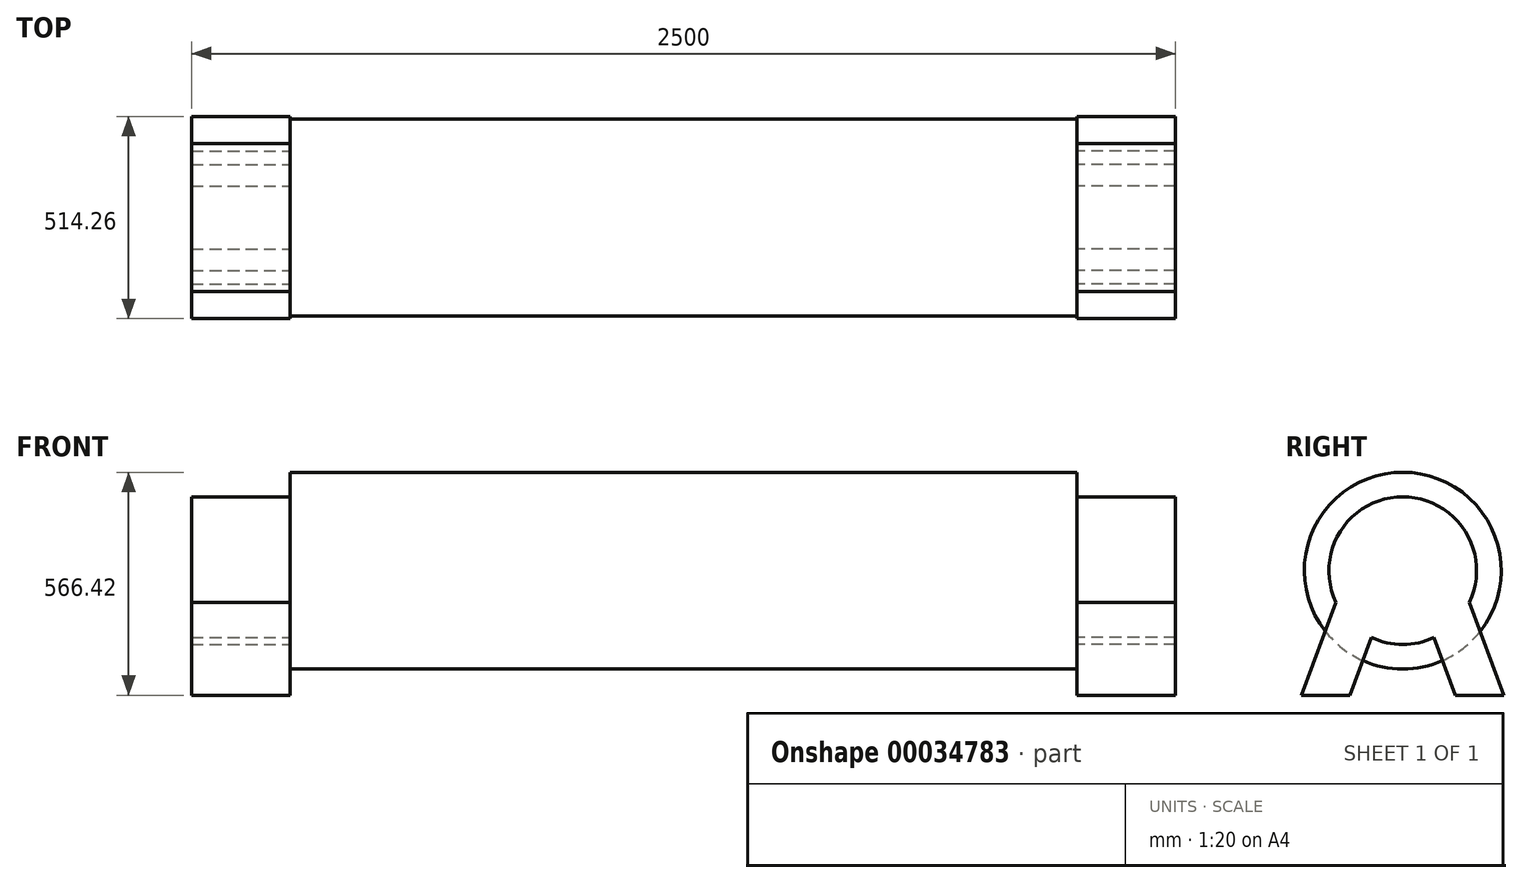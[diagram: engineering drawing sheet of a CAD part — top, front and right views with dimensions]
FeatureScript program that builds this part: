
annotation { "Feature Type Name" : "Feature", "Feature Type Description" : "" }
export const myFeature = defineFeature(function(context is Context, id is Id, definition is map)
    precondition{}
    {
        {
            var Q0;
            Q0=qCreatedBy(makeId("Right.planeOp"),FACE);
            var sketch = newSketch(context, id + "F0", { "sketchPlane" : qUnion([Q0])});
            skCircle(sketch, "E0", {"center": v(0, 0) * mm, "radius": 250 * mm});
            skSolve(sketch);
        }
        {
            var Q0;
            Q0=makeQuery(id+"F0.imprint","IMPRINT",FACE,{"disambiguationData":[TD([[makeQuery(id+"F0.imprint","IMPRINT",EDGE,{"derivedFrom":sQuery(id+"F0.wireOp",EDGE,"E0")}),1.0]])]});
            extrude(context, id + "F1", {"entities" : qUnion([Q0]), "depth" : 2000 * mm});
        }
        {
            var Q0;
            Q0=makeQuery(id+"F1.opExtrude","CAP_FACE",FACE,{"disambiguationData":[OSD([sQuery(id+"F0.wireOp",EDGE,"E0")])],"isStart":false});
            var sketch = newSketch(context, id + "F2", { "sketchPlane" : qUnion([Q0])});
            skCircle(sketch, "E1", {"center": v(0, 0) * mm, "radius": 125 * mm});
            skSolve(sketch);
        }
        {
            var Q0;
            Q0=makeQuery(id+"F2.imprint","IMPRINT",FACE,{"disambiguationData":[TD([[makeQuery(id+"F2.imprint","IMPRINT",EDGE,{"derivedFrom":sQuery(id+"F2.wireOp",EDGE,"E1")}),1.0]])]});
            extrude(context, id + "F3", {"entities" : qUnion([Q0]), "operationType" : NewBodyOperationType.ADD, "depth" : 250 * mm, "hasSecondDirection" : true, "secondDirectionOppositeDirection" : true, "secondDirectionDepth" : 2250 * mm});
        }
        {
            var Q0;
            Q0=makeQuery(id+"F1.opExtrude","CAP_FACE",FACE,{"disambiguationData":[OSD([sQuery(id+"F0.wireOp",EDGE,"E0")])],"isStart":false});
            var sketch = newSketch(context, id + "F4", { "sketchPlane" : qUnion([Q0])});
            skCircle(sketch, "E2", {"center": v(0, 0) * mm, "radius": 187.5 * mm});
            skLineSegment(sketch, "E3", {"start": v(-169.32, -80.55) * mm, "end": v(-257.13, -316.42) * mm});
            skLineSegment(sketch, "E4", {"start": v(-257.13, -316.42) * mm, "end": v(-134.25, -316.42) * mm});
            skLineSegment(sketch, "E5", {"start": v(-134.25, -316.42) * mm, "end": v(-79.64, -169.74) * mm});
            skLineSegment(sketch, "E6", {"start": v(0, 0) * mm, "end": v(0, -613.8) * mm, "construction": true});
            skLineSegment(sketch, "E7.MirrorCS", {"start": v(257.13, -316.42) * mm, "end": v(134.25, -316.42) * mm});
            skLineSegment(sketch, "E8.MirrorCS", {"start": v(169.32, -80.55) * mm, "end": v(257.13, -316.42) * mm});
            skLineSegment(sketch, "E9.MirrorCS", {"start": v(134.25, -316.42) * mm, "end": v(79.64, -169.74) * mm});
            skLineSegment(sketch, "E10", {"start": v(0, -316.42) * mm, "end": v(0, 250) * mm, "construction": true});
            skSolve(sketch);
        }
        {
            var Q0;
            {var subQ5=sQuery(id+"F4.wireOp",EDGE,"E4");Q0=makeQuery(id+"F4.imprint","IMPRINT",FACE,{"disambiguationData":[TD([[makeQuery(id+"F4.imprint","IMPRINT",EDGE,{"derivedFrom":subQ5}),1.0]])]});}
            var Q1;
            {var subQ5=sQuery(id+"F4.wireOp",EDGE,"E7.MirrorCS");Q1=makeQuery(id+"F4.imprint","IMPRINT",FACE,{"disambiguationData":[TD([[makeQuery(id+"F4.imprint","IMPRINT",EDGE,{"derivedFrom":subQ5}),-1.0]])]});}
            var Q2;
            {var subQ3=sQuery(id+"F4.wireOp",EDGE,"E8.MirrorCS");var subQ5=sQuery(id+"F4.wireOp",EDGE,"E2");var subQ7=makeQuery(id+"F4.imprint","INTERSECT",VERTEX,{"derivedFrom":[subQ5,subQ3]});Q2=makeQuery(id+"F4.imprint","IMPRINT",FACE,{"disambiguationData":[TD([[makeQuery(id+"F4.imprint","IMPRINT",EDGE,{"disambiguationData":[TD([[subQ7,1.0]])],"derivedFrom":subQ5}),-1.0]])]});}
            var Q3;
            Q3=makeQuery(id+"F4.imprint","IMPRINT",FACE,{"disambiguationData":[TD([[makeQuery(id+"F4.imprint","IMPRINT",EDGE,{"derivedFrom":makeQuery(id+"F3.boolean.opBoolean","INTERSECT",EDGE,{"derivedFrom":[makeQuery(id+"F1.opExtrude","CAP_FACE",FACE,{"disambiguationData":[OSD([sQuery(id+"F0.wireOp",EDGE,"E0")])],"isStart":false}),makeQuery(id+"F3.opExtrude","SWEPT_FACE",FACE,{"disambiguationData":[OSD([sQuery(id+"F2.wireOp",EDGE,"E1")])]})]})}),1.0]])]});
            var Q4;
            {var subQ3=sQuery(id+"F4.wireOp",EDGE,"E3");var subQ5=sQuery(id+"F4.wireOp",EDGE,"E2");var subQ7=makeQuery(id+"F4.imprint","INTERSECT",VERTEX,{"derivedFrom":[subQ5,subQ3]});Q4=makeQuery(id+"F4.imprint","IMPRINT",FACE,{"disambiguationData":[TD([[makeQuery(id+"F4.imprint","IMPRINT",EDGE,{"disambiguationData":[TD([[subQ7,-1.0]])],"derivedFrom":subQ5}),-1.0]])]});}
            extrude(context, id + "F5", {"entities" : qUnion([Q0, Q1, Q2, Q3, Q4]), "operationType" : NewBodyOperationType.ADD, "depth" : 250 * mm});
        }
        {
            var Q0;
            Q0=makeQuery(id+"F1.opExtrude","CAP_FACE",FACE,{"disambiguationData":[OSD([sQuery(id+"F0.wireOp",EDGE,"E0")])],"isStart":true});
            var sketch = newSketch(context, id + "F6", { "sketchPlane" : qUnion([Q0])});
            skLineSegment(sketch, "E11", {"start": v(-169.32, -80.55) * mm, "end": v(-257.13, -316.42) * mm});
            skCircle(sketch, "E12", {"center": v(0, 0) * mm, "radius": 187.5 * mm});
            skLineSegment(sketch, "E13", {"start": v(-257.13, -316.42) * mm, "end": v(-134.25, -316.42) * mm});
            skLineSegment(sketch, "E14", {"start": v(-134.25, -316.42) * mm, "end": v(-79.64, -169.74) * mm});
            skLineSegment(sketch, "E15", {"start": v(0, 0) * mm, "end": v(0, -352.78) * mm, "construction": true});
            skLineSegment(sketch, "E16.MirrorCS", {"start": v(257.13, -316.42) * mm, "end": v(134.25, -316.42) * mm});
            skLineSegment(sketch, "E17.MirrorCS", {"start": v(169.32, -80.55) * mm, "end": v(257.13, -316.42) * mm});
            skLineSegment(sketch, "E18.MirrorCS", {"start": v(134.25, -316.42) * mm, "end": v(79.64, -169.74) * mm});
            skSolve(sketch);
        }
        {
            var Q0;
            {var subQ5=sQuery(id+"F6.wireOp",EDGE,"E13");Q0=makeQuery(id+"F6.imprint","IMPRINT",FACE,{"disambiguationData":[TD([[makeQuery(id+"F6.imprint","IMPRINT",EDGE,{"derivedFrom":subQ5}),1.0]])]});}
            var Q1;
            {var subQ5=sQuery(id+"F6.wireOp",EDGE,"E16.MirrorCS");Q1=makeQuery(id+"F6.imprint","IMPRINT",FACE,{"disambiguationData":[TD([[makeQuery(id+"F6.imprint","IMPRINT",EDGE,{"derivedFrom":subQ5}),-1.0]])]});}
            var Q2;
            {var subQ3=sQuery(id+"F6.wireOp",EDGE,"E17.MirrorCS");var subQ5=sQuery(id+"F6.wireOp",EDGE,"E12");var subQ7=makeQuery(id+"F6.imprint","INTERSECT",VERTEX,{"derivedFrom":[subQ5,subQ3]});Q2=makeQuery(id+"F6.imprint","IMPRINT",FACE,{"disambiguationData":[TD([[makeQuery(id+"F6.imprint","IMPRINT",EDGE,{"disambiguationData":[TD([[subQ7,1.0]])],"derivedFrom":subQ5}),-1.0]])]});}
            var Q3;
            {var subQ3=sQuery(id+"F6.wireOp",EDGE,"E12");var subQ5=sQuery(id+"F6.wireOp",EDGE,"E11");var subQ7=makeQuery(id+"F6.imprint","INTERSECT",VERTEX,{"derivedFrom":[subQ5,subQ3]});Q3=makeQuery(id+"F6.imprint","IMPRINT",FACE,{"disambiguationData":[TD([[makeQuery(id+"F6.imprint","IMPRINT",EDGE,{"disambiguationData":[TD([[subQ7,-1.0]])],"derivedFrom":subQ5}),1.0]])]});}
            var Q4;
            Q4=makeQuery(id+"F6.imprint","IMPRINT",FACE,{"disambiguationData":[TD([[makeQuery(id+"F6.imprint","IMPRINT",EDGE,{"derivedFrom":makeQuery(id+"F3.boolean.opBoolean","INTERSECT",EDGE,{"derivedFrom":[makeQuery(id+"F1.opExtrude","CAP_FACE",FACE,{"disambiguationData":[OSD([sQuery(id+"F0.wireOp",EDGE,"E0")])],"isStart":true}),makeQuery(id+"F3.opExtrude","SWEPT_FACE",FACE,{"disambiguationData":[OSD([sQuery(id+"F2.wireOp",EDGE,"E1")])]})]})}),-1.0]])]});
            extrude(context, id + "F7", {"entities" : qUnion([Q0, Q1, Q2, Q3, Q4]), "operationType" : NewBodyOperationType.ADD, "depth" : 250 * mm});
        }
    });
